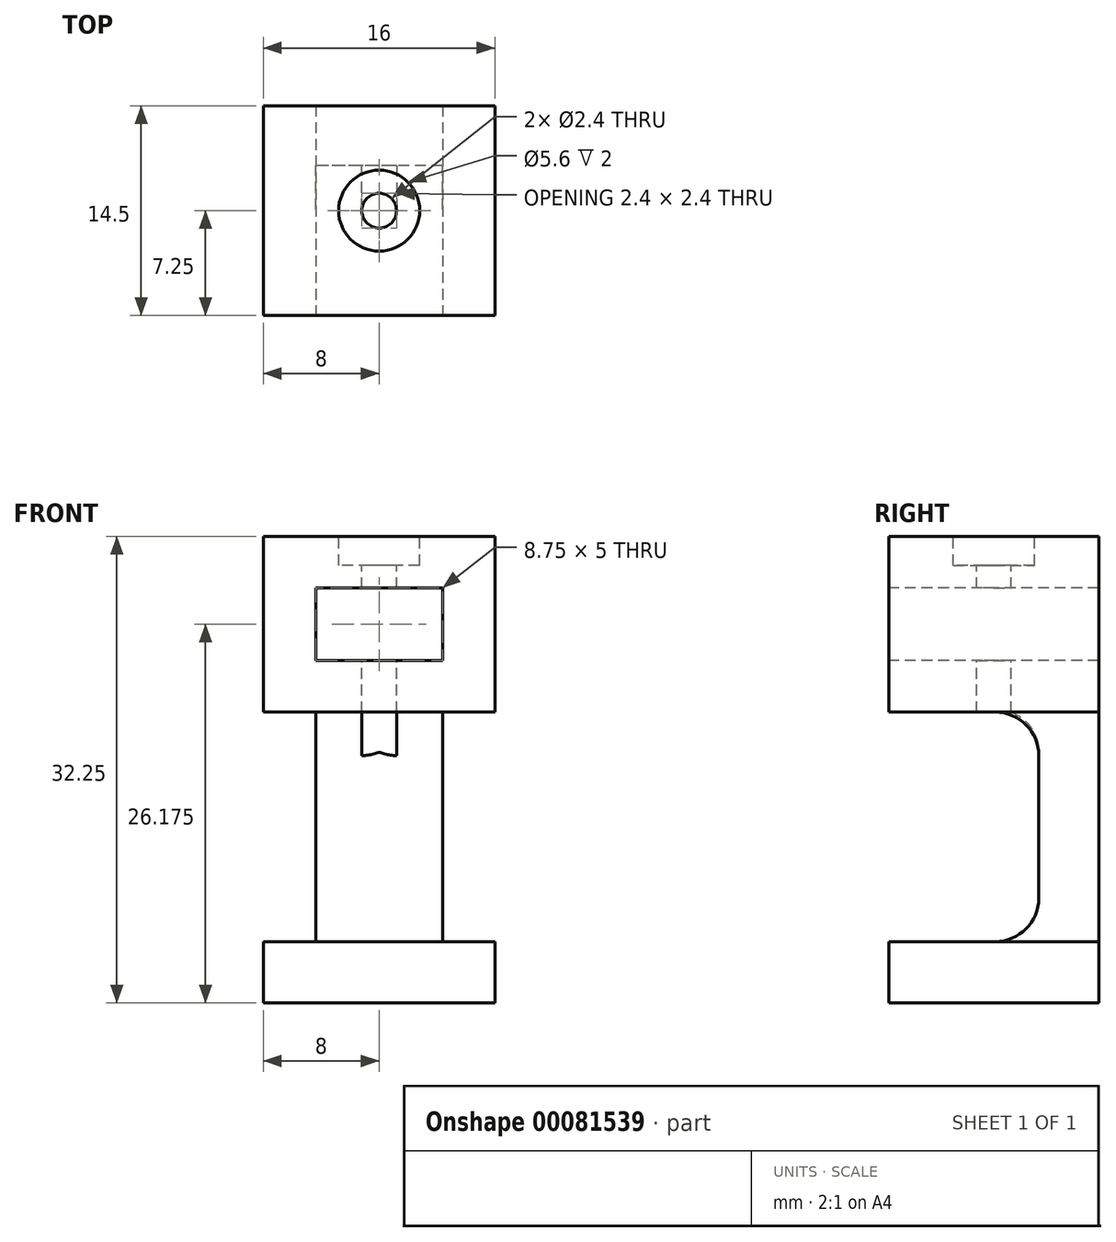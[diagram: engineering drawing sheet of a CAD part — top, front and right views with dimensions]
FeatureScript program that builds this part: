
annotation { "Feature Type Name" : "Feature", "Feature Type Description" : "" }
export const myFeature = defineFeature(function(context is Context, id is Id, definition is map)
    precondition{}
    {
        {
            var Q0;
            Q0=qCreatedBy(makeId("Top.planeOp"),FACE);
            var sketch = newSketch(context, id + "F0", { "sketchPlane" : qUnion([Q0])});
            skLineSegment(sketch, "E0.bottom", {"start": v(-8, 7.25) * mm, "end": v(8, 7.25) * mm});
            skLineSegment(sketch, "E0.top", {"start": v(-8, -7.25) * mm, "end": v(8, -7.25) * mm});
            skLineSegment(sketch, "E0.left", {"start": v(-8, 7.25) * mm, "end": v(-8, -7.25) * mm});
            skLineSegment(sketch, "E0.right", {"start": v(8, 7.25) * mm, "end": v(8, -7.25) * mm});
            skPoint(sketch, "E0.middle", {"position": v(0, 0) * mm});
            skSolve(sketch);
        }
        {
            var Q0;
            Q0=qSketchRegion(id+"F0",true);
            extrude(context, id + "F1", {"entities" : qUnion([Q0]), "depth" : 32.25 * mm});
        }
        {
            var Q0;
            Q0=makeQuery(id+"F1.opExtrude","SWEPT_FACE",FACE,{"disambiguationData":[OSD([sQuery(id+"F0.wireOp",EDGE,"E0.top")])]});
            var sketch = newSketch(context, id + "F2", { "sketchPlane" : qUnion([Q0])});
            skLineSegment(sketch, "E1", {"start": v(-8, 20.1) * mm, "end": v(8, 20.1) * mm, "construction": true});
            skLineSegment(sketch, "E2", {"start": v(-8, 4.25) * mm, "end": v(8, 4.25) * mm, "construction": true});
            skLineSegment(sketch, "E3", {"start": v(-4.38, 20.1) * mm, "end": v(-4.38, 4.25) * mm});
            skLineSegment(sketch, "E4", {"start": v(4.37, 20.1) * mm, "end": v(4.37, 4.25) * mm});
            skLineSegment(sketch, "E5", {"start": v(-8, 4.25) * mm, "end": v(8, 4.25) * mm});
            skLineSegment(sketch, "E6", {"start": v(-8, 20.1) * mm, "end": v(-4.38, 20.1) * mm});
            skLineSegment(sketch, "E7", {"start": v(4.37, 20.1) * mm, "end": v(8, 20.1) * mm});
            skSolve(sketch);
        }
        {
            var Q0;
            {var subQ0=sQuery(id+"F2.wireOp",EDGE,"E3");Q0=makeQuery(id+"F2.imprint","IMPRINT",FACE,{"disambiguationData":[TD([[makeQuery(id+"F2.imprint","IMPRINT",EDGE,{"derivedFrom":subQ0}),-1.0]])]});}
            var Q1;
            {var subQ0=sQuery(id+"F2.wireOp",EDGE,"E4");Q1=makeQuery(id+"F2.imprint","IMPRINT",FACE,{"disambiguationData":[TD([[makeQuery(id+"F2.imprint","IMPRINT",EDGE,{"derivedFrom":subQ0}),1.0]])]});}
            extrude(context, id + "F3", {"entities" : qUnion([Q0, Q1]), "operationType" : NewBodyOperationType.REMOVE, "oppositeDirection" : true, "depth" : 15.25 * mm});
        }
        {
            var Q0;
            Q0=makeQuery(id+"F3.boolean.opBoolean","COPY",FACE,{"derivedFrom":makeQuery(id+"F3.opExtrude","SWEPT_FACE",FACE,{"disambiguationData":[OSD([sQuery(id+"F2.wireOp",EDGE,"E3")])]})});
            var sketch = newSketch(context, id + "F4", { "sketchPlane" : qUnion([Q0])});
            skLineSegment(sketch, "E8.bottom", {"start": v(7.25, 20.1) * mm, "end": v(-3.1, 20.1) * mm});
            skLineSegment(sketch, "E8.top", {"start": v(7.25, 4.25) * mm, "end": v(-3.1, 4.25) * mm});
            skLineSegment(sketch, "E8.left", {"start": v(7.25, 20.1) * mm, "end": v(7.25, 4.25) * mm});
            skLineSegment(sketch, "E8.right", {"start": v(-3.1, 20.1) * mm, "end": v(-3.1, 4.25) * mm});
            skSolve(sketch);
        }
        {
            var Q0;
            Q0=makeQuery(id+"F4.imprint","IMPRINT",FACE,{"disambiguationData":[TD([[makeQuery(id+"F4.imprint","IMPRINT",EDGE,{"derivedFrom":sQuery(id+"F4.wireOp",EDGE,"E8.bottom")}),-1.0]])]});
            extrude(context, id + "F5", {"entities" : qUnion([Q0]), "operationType" : NewBodyOperationType.REMOVE, "oppositeDirection" : true, "depth" : 16 * mm});
        }
        {
            var Q0;
            {var subQ2=sQuery(id+"F0.wireOp",EDGE,"E0.top");Q0=makeQuery(id+"F5.boolean.opBoolean","SPLIT",FACE,{"disambiguationData":[TD([makeQuery(id+"F3.boolean.opBoolean","COPY",FACE,{"derivedFrom":makeQuery(id+"F3.opExtrude","SWEPT_FACE",FACE,{"disambiguationData":[OSD([sQuery(id+"F2.wireOp",EDGE,"E6")])]})})])],"derivedFrom":makeQuery(id+"F1.opExtrude","SWEPT_FACE",FACE,{"disambiguationData":[OSD([subQ2])]})});}
            var sketch = newSketch(context, id + "F6", { "sketchPlane" : qUnion([Q0])});
            skLineSegment(sketch, "E9", {"start": v(-8, 20.1) * mm, "end": v(8, 32.25) * mm, "construction": true});
            skLineSegment(sketch, "E10", {"start": v(-8, 32.25) * mm, "end": v(8, 20.1) * mm, "construction": true});
            skPoint(sketch, "E11", {"position": v(0, 26.18) * mm});
            skLineSegment(sketch, "E12.bottom", {"start": v(-4.38, 28.67) * mm, "end": v(4.37, 28.67) * mm});
            skLineSegment(sketch, "E12.top", {"start": v(-4.38, 23.67) * mm, "end": v(4.37, 23.67) * mm});
            skLineSegment(sketch, "E12.left", {"start": v(-4.38, 28.67) * mm, "end": v(-4.38, 23.67) * mm});
            skLineSegment(sketch, "E12.right", {"start": v(4.37, 28.67) * mm, "end": v(4.37, 23.67) * mm});
            skSolve(sketch);
        }
        {
            var Q0;
            Q0=makeQuery(id+"F6.imprint","IMPRINT",FACE,{"disambiguationData":[TD([[makeQuery(id+"F6.imprint","IMPRINT",EDGE,{"derivedFrom":sQuery(id+"F6.wireOp",EDGE,"E12.bottom")}),-1.0]])]});
            extrude(context, id + "F7", {"entities" : qUnion([Q0]), "operationType" : NewBodyOperationType.REMOVE, "oppositeDirection" : true, "depth" : 14.5 * mm});
        }
        {
            var Q0;
            Q0=makeQuery(id+"F1.opExtrude","CAP_FACE",FACE,{"disambiguationData":[OSD([sQuery(id+"F0.wireOp",EDGE,"E0.bottom"),sQuery(id+"F0.wireOp",EDGE,"E0.top"),sQuery(id+"F0.wireOp",EDGE,"E0.left"),sQuery(id+"F0.wireOp",EDGE,"E0.right")])],"isStart":false});
            var sketch = newSketch(context, id + "F8", { "sketchPlane" : qUnion([Q0])});
            skCircle(sketch, "E13", {"center": v(0, 0) * mm, "radius": 2.8 * mm});
            skCircle(sketch, "E14", {"center": v(0, 0) * mm, "radius": 1.2 * mm});
            skSolve(sketch);
        }
        {
            var Q0;
            Q0=makeQuery(id+"F8.imprint","IMPRINT",FACE,{"disambiguationData":[TD([[makeQuery(id+"F8.imprint","IMPRINT",EDGE,{"derivedFrom":sQuery(id+"F8.wireOp",EDGE,"E13")}),1.0]])]});
            extrude(context, id + "F9", {"entities" : qUnion([Q0]), "operationType" : NewBodyOperationType.REMOVE, "oppositeDirection" : true, "depth" : 2 * mm});
        }
        {
            var Q0;
            Q0=makeQuery(id+"F9.boolean.opBoolean","SPLIT",FACE,{"disambiguationData":[TD([makeQuery(id+"F9.opExtrude","SWEPT_FACE",FACE,{"disambiguationData":[OSD([sQuery(id+"F8.wireOp",EDGE,"E14")])]})])],"derivedFrom":makeQuery(id+"F1.opExtrude","CAP_FACE",FACE,{"disambiguationData":[OSD([sQuery(id+"F0.wireOp",EDGE,"E0.bottom"),sQuery(id+"F0.wireOp",EDGE,"E0.top"),sQuery(id+"F0.wireOp",EDGE,"E0.left"),sQuery(id+"F0.wireOp",EDGE,"E0.right")])],"isStart":false})});
            extrude(context, id + "F10", {"entities" : qUnion([Q0]), "operationType" : NewBodyOperationType.REMOVE, "oppositeDirection" : true, "depth" : 12.5 * mm});
        }
        {
            var Q0;
            Q0=makeQuery(id+"F5.boolean.opBoolean","COPY",EDGE,{"derivedFrom":makeQuery(id+"F5.opExtrude","SWEPT_EDGE",EDGE,{"disambiguationData":[OSD([sQuery(id+"F2.wireOp",EDGE,"E3"),sQuery(id+"F2.wireOp",EDGE,"E6"),sQuery(id+"F4.wireOp",EDGE,"E8.bottom"),sQuery(id+"F4.wireOp",EDGE,"E8.right")])]})});
            var Q1;
            Q1=makeQuery(id+"F5.boolean.opBoolean","COPY",EDGE,{"derivedFrom":makeQuery(id+"F5.opExtrude","SWEPT_EDGE",EDGE,{"disambiguationData":[OSD([sQuery(id+"F2.wireOp",EDGE,"E3"),sQuery(id+"F2.wireOp",EDGE,"E5"),sQuery(id+"F4.wireOp",EDGE,"E8.top"),sQuery(id+"F4.wireOp",EDGE,"E8.right")])]})});
            fillet(context, id + "F11", {"entities" : qUnion([Q0, Q1]), "radius" : 3 * mm, "tangentPropagation" : true, "allowEdgeOverflow" : false});
        }
    });
